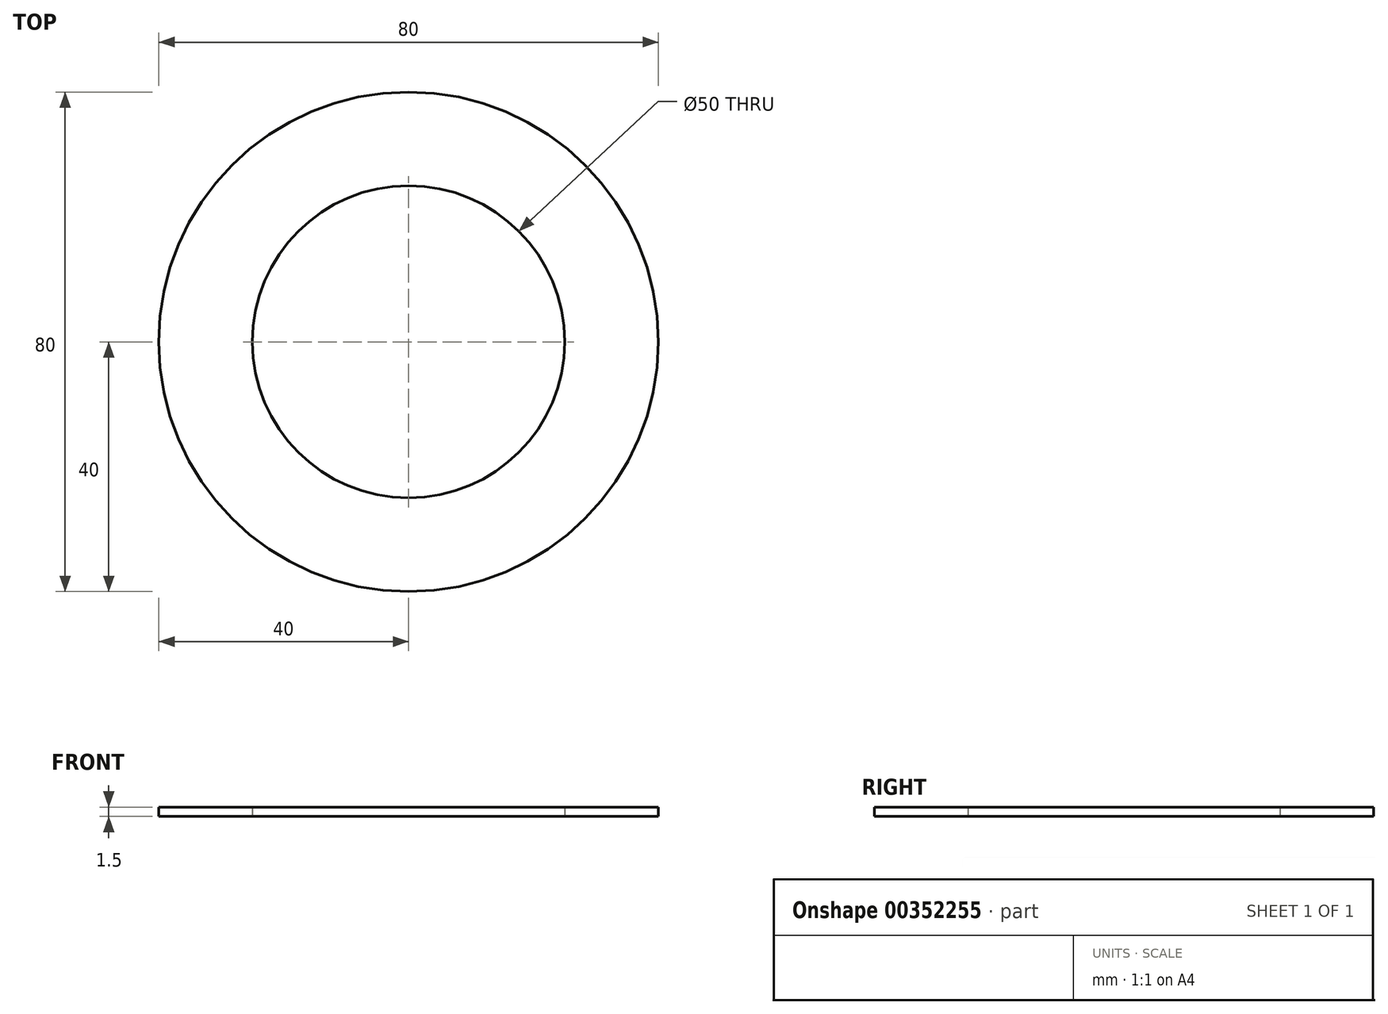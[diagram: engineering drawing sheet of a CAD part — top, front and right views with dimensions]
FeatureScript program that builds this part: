
annotation { "Feature Type Name" : "Feature", "Feature Type Description" : "" }
export const myFeature = defineFeature(function(context is Context, id is Id, definition is map)
    precondition{}
    {
        {
            var Q0;
            Q0=qCreatedBy(makeId("Top.planeOp"),FACE);
            var sketch = newSketch(context, id + "F0", { "sketchPlane" : qUnion([Q0])});
            skCircle(sketch, "E0", {"center": v(0, 0) * mm, "radius": 25 * mm});
            skCircle(sketch, "E1", {"center": v(0, 0) * mm, "radius": 40 * mm});
            skSolve(sketch);
        }
        {
            var Q0;
            Q0=makeQuery(id+"F0.imprint","IMPRINT",FACE,{"disambiguationData":[TD([[makeQuery(id+"F0.imprint","IMPRINT",EDGE,{"derivedFrom":sQuery(id+"F0.wireOp",EDGE,"E0")}),-1.0]])]});
            extrude(context, id + "F1", {"entities" : qUnion([Q0]), "depth" : 1.5 * mm, "offsetDistance" : 25 * mm});
        }
    });
